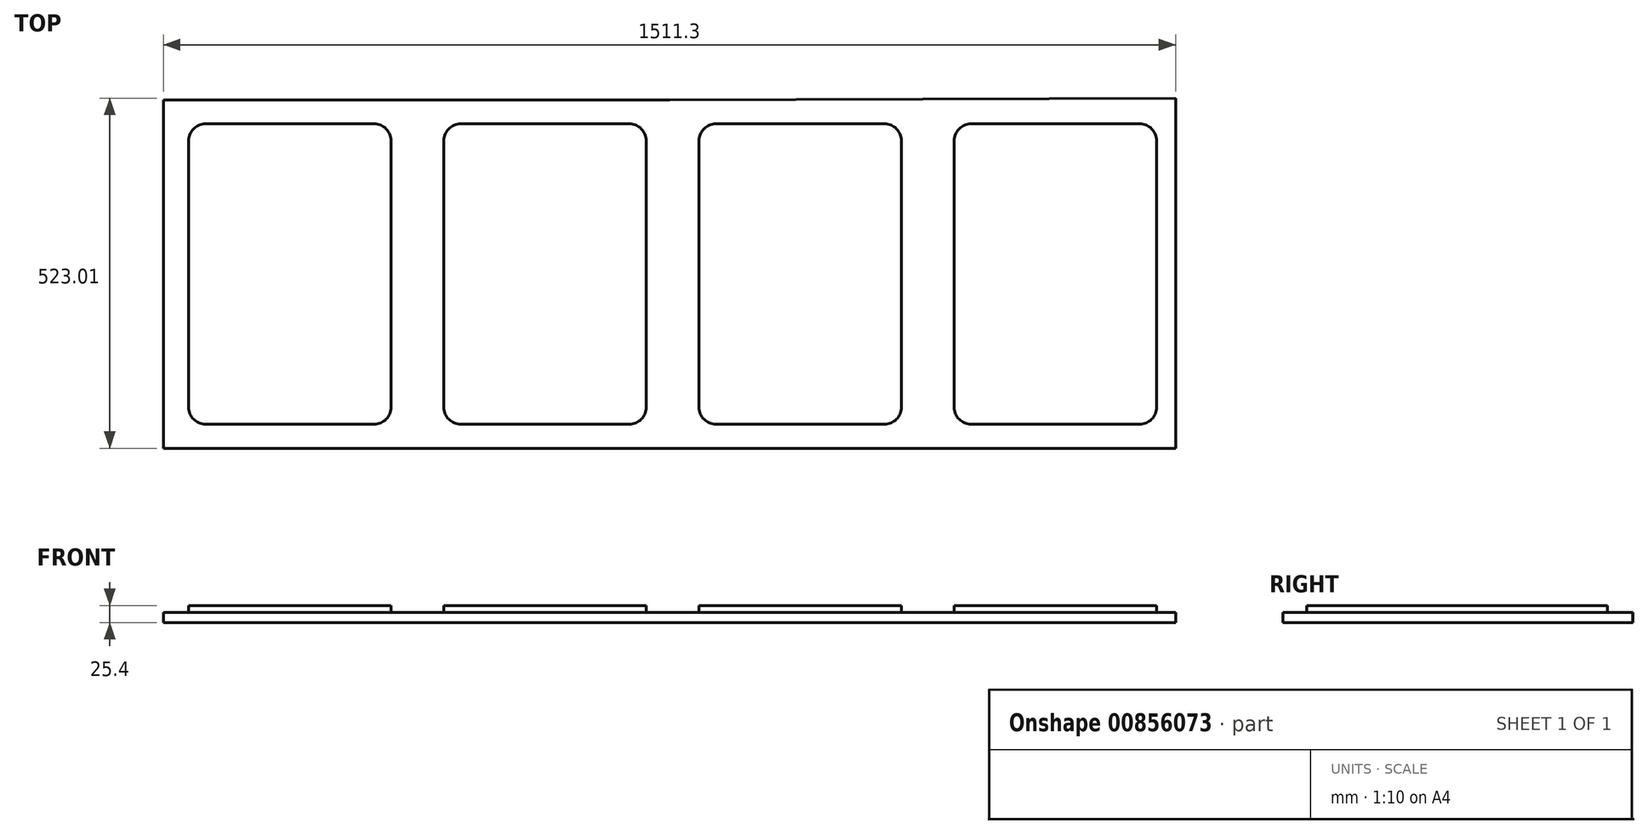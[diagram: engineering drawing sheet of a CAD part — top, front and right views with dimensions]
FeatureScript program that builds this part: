
annotation { "Feature Type Name" : "Feature", "Feature Type Description" : "" }
export const myFeature = defineFeature(function(context is Context, id is Id, definition is map)
    precondition{}
    {
        {
            var Q0;
            Q0=qCreatedBy(makeId("Top.planeOp"),FACE);
            var sketch = newSketch(context, id + "F0", { "sketchPlane" : qUnion([Q0])});
            skLineSegment(sketch, "E0.left", {"start": v(-756.07, 292.14) * mm, "end": v(-756.07, -228.56) * mm});
            skLineSegment(sketch, "E0.right", {"start": v(755.23, 294.43) * mm, "end": v(755.23, -228.58) * mm});
            skLineSegment(sketch, "E1", {"start": v(-0.42, 292.14) * mm, "end": v(-0.42, -228.58) * mm});
            skLineSegment(sketch, "E2", {"start": v(-378.24, 292.14) * mm, "end": v(-375.88, -225.89) * mm});
            skLineSegment(sketch, "E3", {"start": v(-756.07, 292.14) * mm, "end": v(-0.42, 292.14) * mm});
            skLineSegment(sketch, "E4", {"start": v(-0.42, 292.14) * mm, "end": v(755.23, 294.43) * mm});
            skLineSegment(sketch, "E5", {"start": v(755.23, -228.58) * mm, "end": v(-0.42, -228.58) * mm});
            skLineSegment(sketch, "E6", {"start": v(-0.42, -228.58) * mm, "end": v(-756.07, -228.56) * mm});
            skLineSegment(sketch, "E7", {"start": v(377.4, 293.28) * mm, "end": v(377.4, -228.58) * mm});
            skLineSegment(sketch, "E8.bottom", {"start": v(-692.86, 256.3) * mm, "end": v(-441.46, 256.3) * mm});
            skLineSegment(sketch, "E8.top", {"start": v(-692.86, -192.72) * mm, "end": v(-441.46, -192.72) * mm});
            skLineSegment(sketch, "E8.left", {"start": v(-718.26, 230.9) * mm, "end": v(-718.26, -167.32) * mm});
            skLineSegment(sketch, "E8.right", {"start": v(-416.06, 230.9) * mm, "end": v(-416.06, -167.32) * mm});
            skLineSegment(sketch, "E9", {"start": v(-416.06, 256.3) * mm, "end": v(-378.24, 292.14) * mm, "construction": true});
            skLineSegment(sketch, "E10", {"start": v(-718.26, 256.3) * mm, "end": v(-756.07, 292.14) * mm, "construction": true});
            skLineSegment(sketch, "E11", {"start": v(-718.26, -192.72) * mm, "end": v(-756.07, -228.56) * mm, "construction": true});
            skLineSegment(sketch, "E12", {"start": v(-416.06, -192.72) * mm, "end": v(-375.88, -225.89) * mm, "construction": true});
            skPoint(sketch, "E13.visualSharp", {"position": v(-718.26, 256.3) * mm});
            skArc(sketch, "E13.filletArc", {"start": v(-692.86, 256.3) * mm, "mid": v(-710.82, 248.86) * mm, "end": v(-718.26, 230.9) * mm});
            skPoint(sketch, "E14.visualSharp", {"position": v(-416.06, 256.3) * mm});
            skArc(sketch, "E14.filletArc", {"start": v(-416.06, 230.9) * mm, "mid": v(-423.5, 248.86) * mm, "end": v(-441.46, 256.3) * mm});
            skPoint(sketch, "E15.visualSharp", {"position": v(-416.06, -192.72) * mm});
            skArc(sketch, "E15.filletArc", {"start": v(-441.46, -192.72) * mm, "mid": v(-423.5, -185.28) * mm, "end": v(-416.06, -167.32) * mm});
            skPoint(sketch, "E16.visualSharp", {"position": v(-718.26, -192.72) * mm});
            skArc(sketch, "E16.filletArc", {"start": v(-718.26, -167.32) * mm, "mid": v(-710.82, -185.28) * mm, "end": v(-692.86, -192.72) * mm});
            skLineSegment(sketch, "E17.1.0.0", {"start": v(-337.26, 230.9) * mm, "end": v(-337.26, -167.32) * mm});
            skArc(sketch, "E17.1.0.1", {"start": v(-311.86, 256.3) * mm, "mid": v(-329.82, 248.86) * mm, "end": v(-337.26, 230.9) * mm});
            skLineSegment(sketch, "E17.1.0.2", {"start": v(-311.86, 256.3) * mm, "end": v(-60.46, 256.3) * mm});
            skArc(sketch, "E17.1.0.3", {"start": v(-35.06, 230.9) * mm, "mid": v(-42.5, 248.86) * mm, "end": v(-60.46, 256.3) * mm});
            skLineSegment(sketch, "E17.1.0.4", {"start": v(-35.06, 230.9) * mm, "end": v(-35.06, -167.32) * mm});
            skLineSegment(sketch, "E17.1.0.5", {"start": v(-311.86, -192.72) * mm, "end": v(-60.46, -192.72) * mm});
            skArc(sketch, "E17.1.0.6", {"start": v(-60.46, -192.72) * mm, "mid": v(-42.5, -185.28) * mm, "end": v(-35.06, -167.32) * mm});
            skArc(sketch, "E17.1.0.7", {"start": v(-337.26, -167.32) * mm, "mid": v(-329.82, -185.28) * mm, "end": v(-311.86, -192.72) * mm});
            skLineSegment(sketch, "E17.2.0.0", {"start": v(43.74, 230.9) * mm, "end": v(43.74, -167.32) * mm});
            skArc(sketch, "E17.2.0.1", {"start": v(69.14, 256.3) * mm, "mid": v(51.18, 248.86) * mm, "end": v(43.74, 230.9) * mm});
            skLineSegment(sketch, "E17.2.0.2", {"start": v(69.14, 256.3) * mm, "end": v(320.54, 256.3) * mm});
            skArc(sketch, "E17.2.0.3", {"start": v(345.94, 230.9) * mm, "mid": v(338.5, 248.86) * mm, "end": v(320.54, 256.3) * mm});
            skLineSegment(sketch, "E17.2.0.4", {"start": v(345.94, 230.9) * mm, "end": v(345.94, -167.32) * mm});
            skLineSegment(sketch, "E17.2.0.5", {"start": v(69.14, -192.72) * mm, "end": v(320.54, -192.72) * mm});
            skArc(sketch, "E17.2.0.6", {"start": v(320.54, -192.72) * mm, "mid": v(338.5, -185.28) * mm, "end": v(345.94, -167.32) * mm});
            skArc(sketch, "E17.2.0.7", {"start": v(43.74, -167.32) * mm, "mid": v(51.18, -185.28) * mm, "end": v(69.14, -192.72) * mm});
            skLineSegment(sketch, "E17.3.0.0", {"start": v(424.74, 230.9) * mm, "end": v(424.74, -167.32) * mm});
            skArc(sketch, "E17.3.0.1", {"start": v(450.14, 256.3) * mm, "mid": v(432.18, 248.86) * mm, "end": v(424.74, 230.9) * mm});
            skLineSegment(sketch, "E17.3.0.2", {"start": v(450.14, 256.3) * mm, "end": v(701.54, 256.3) * mm});
            skArc(sketch, "E17.3.0.3", {"start": v(726.94, 230.9) * mm, "mid": v(719.5, 248.86) * mm, "end": v(701.54, 256.3) * mm});
            skLineSegment(sketch, "E17.3.0.4", {"start": v(726.94, 230.9) * mm, "end": v(726.94, -167.32) * mm});
            skLineSegment(sketch, "E17.3.0.5", {"start": v(450.14, -192.72) * mm, "end": v(701.54, -192.72) * mm});
            skArc(sketch, "E17.3.0.6", {"start": v(701.54, -192.72) * mm, "mid": v(719.5, -185.28) * mm, "end": v(726.94, -167.32) * mm});
            skArc(sketch, "E17.3.0.7", {"start": v(424.74, -167.32) * mm, "mid": v(432.18, -185.28) * mm, "end": v(450.14, -192.72) * mm});
            skLineSegment(sketch, "E17.direction1", {"start": v(-718.26, -167.32) * mm, "end": v(-337.26, -167.32) * mm, "construction": true});
            skSolve(sketch);
        }
        {
            var Q0;
            {var subQ1=sQuery(id+"F0.wireOp",EDGE,"E0.left");Q0=makeQuery(id+"F0.imprint","IMPRINT",FACE,{"disambiguationData":[TD([[makeQuery(id+"F0.imprint","IMPRINT",EDGE,{"derivedFrom":subQ1}),1.0]])]});}
            var Q1;
            {var subQ0=sQuery(id+"F0.wireOp",EDGE,"E1");Q1=makeQuery(id+"F0.imprint","IMPRINT",FACE,{"disambiguationData":[TD([[makeQuery(id+"F0.imprint","IMPRINT",EDGE,{"derivedFrom":subQ0}),1.0]])]});}
            var Q2;
            {var subQ0=sQuery(id+"F0.wireOp",EDGE,"E0.right");Q2=makeQuery(id+"F0.imprint","IMPRINT",FACE,{"disambiguationData":[TD([[makeQuery(id+"F0.imprint","IMPRINT",EDGE,{"derivedFrom":subQ0}),-1.0]])]});}
            extrude(context, id + "F1", {"entities" : qUnion([Q0, Q1, Q2]), "depth" : 15.24 * mm});
        }
        {
            var Q0;
            Q0=makeQuery(id+"F0.imprint","IMPRINT",FACE,{"disambiguationData":[TD([[makeQuery(id+"F0.imprint","IMPRINT",EDGE,{"derivedFrom":sQuery(id+"F0.wireOp",EDGE,"E8.bottom")}),-1.0]])]});
            var Q1;
            Q1=makeQuery(id+"F0.imprint","IMPRINT",FACE,{"disambiguationData":[TD([[makeQuery(id+"F0.imprint","IMPRINT",EDGE,{"derivedFrom":sQuery(id+"F0.wireOp",EDGE,"E17.1.0.0")}),1.0]])]});
            var Q2;
            Q2=makeQuery(id+"F0.imprint","IMPRINT",FACE,{"disambiguationData":[TD([[makeQuery(id+"F0.imprint","IMPRINT",EDGE,{"derivedFrom":sQuery(id+"F0.wireOp",EDGE,"E17.2.0.0")}),1.0]])]});
            var Q3;
            Q3=makeQuery(id+"F0.imprint","IMPRINT",FACE,{"disambiguationData":[TD([[makeQuery(id+"F0.imprint","IMPRINT",EDGE,{"derivedFrom":sQuery(id+"F0.wireOp",EDGE,"E17.3.0.0")}),1.0]])]});
            extrude(context, id + "F2", {"entities" : qUnion([Q0, Q1, Q2, Q3]), "operationType" : NewBodyOperationType.ADD, "depth" : 25.4 * mm});
        }
    });
